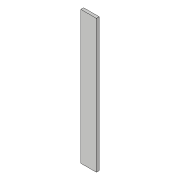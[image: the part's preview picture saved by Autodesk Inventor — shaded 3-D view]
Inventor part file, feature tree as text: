
AUTODESK INVENTOR PART (.ipt)
format: ipt  version: 2018.3 (Build 223284000, 284)  size: 71,168 bytes
history: native  units: in
note: dims shown in document units (in); Inventor stores cm internally (conversion verified against a paired STEP export)
features: extrude x1, sketch x1
ambient origin geometry x8: Origin, YZ Plane, XZ Plane, XY Plane, X Axis, Y Axis, Z Axis, Center Point
bodies: Solid1 (feature_tree)
feature tree (2):
  extrude  "Extrusion1"  Depth=0.7in
  sketch  "Sketch1"  dims[d0=6.0in d1=0.7in d2=0.125in d3=0.0in]
